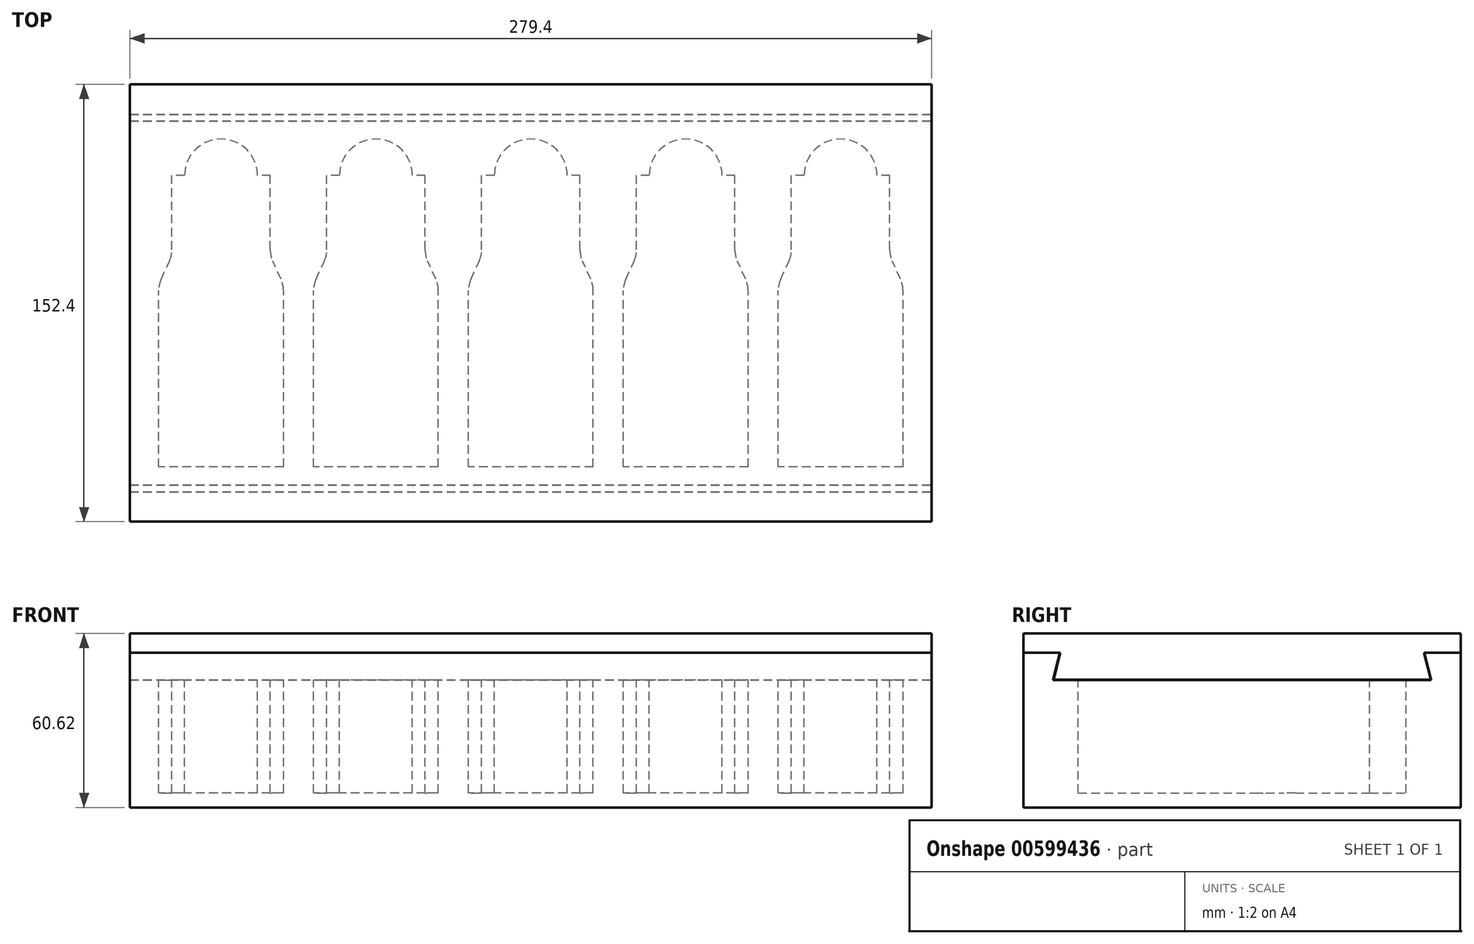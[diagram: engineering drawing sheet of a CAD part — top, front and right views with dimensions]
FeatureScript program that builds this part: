
annotation { "Feature Type Name" : "Feature", "Feature Type Description" : "" }
export const myFeature = defineFeature(function(context is Context, id is Id, definition is map)
    precondition{}
    {
        {
            var Q0;
            Q0=qCreatedBy(makeId("Top.planeOp"),FACE);
            var sketch = newSketch(context, id + "F0", { "sketchPlane" : qUnion([Q0])});
            skLineSegment(sketch, "E0.bottom", {"start": v(139.7, -76.2) * mm, "end": v(-139.7, -76.2) * mm});
            skLineSegment(sketch, "E0.top", {"start": v(139.7, 76.2) * mm, "end": v(-139.7, 76.2) * mm});
            skLineSegment(sketch, "E0.left", {"start": v(139.7, -76.2) * mm, "end": v(139.7, 76.2) * mm});
            skLineSegment(sketch, "E0.right", {"start": v(-139.7, -76.2) * mm, "end": v(-139.7, 76.2) * mm});
            skPoint(sketch, "E0.middle", {"position": v(0, 0) * mm});
            skSolve(sketch);
        }
        {
            var Q0;
            Q0=makeQuery(id+"F0.imprint","IMPRINT",FACE,{"disambiguationData":[TD([[makeQuery(id+"F0.imprint","IMPRINT",EDGE,{"derivedFrom":sQuery(id+"F0.wireOp",EDGE,"E0.bottom")}),-1.0]])]});
            extrude(context, id + "F1", {"entities" : qUnion([Q0]), "depth" : 53.97 * mm, "offsetDistance" : 25.4 * mm});
        }
        {
            var Q0;
            Q0=makeQuery(id+"F1.opExtrude","SWEPT_FACE",FACE,{"disambiguationData":[OSD([sQuery(id+"F0.wireOp",EDGE,"E0.left")])]});
            var sketch = newSketch(context, id + "F2", { "sketchPlane" : qUnion([Q0])});
            skLineSegment(sketch, "E1.top", {"start": v(-65.87, 44.45) * mm, "end": v(65.87, 44.45) * mm});
            skLineSegment(sketch, "E2.bottom", {"start": v(-63.5, 53.98) * mm, "end": v(63.5, 53.98) * mm});
            skLineSegment(sketch, "E3", {"start": v(-65.87, 44.45) * mm, "end": v(-63.5, 53.98) * mm});
            skLineSegment(sketch, "E4", {"start": v(65.87, 44.45) * mm, "end": v(63.5, 53.98) * mm});
            skLineSegment(sketch, "E5", {"start": v(-56.48, 75.32) * mm, "end": v(-56.48, 24.92) * mm, "construction": true});
            skLineSegment(sketch, "E6", {"start": v(-49.45, 53.98) * mm, "end": v(-47.08, 44.45) * mm, "construction": true});
            skSolve(sketch);
        }
        {
            var Q0;
            Q0=makeQuery(id+"F2.imprint","IMPRINT",FACE,{"disambiguationData":[TD([[makeQuery(id+"F2.imprint","IMPRINT",EDGE,{"derivedFrom":sQuery(id+"F2.wireOp",EDGE,"E1.top")}),1.0]])]});
            extrude(context, id + "F3", {"entities" : qUnion([Q0]), "operationType" : NewBodyOperationType.REMOVE, "endBound" : BoundingType.THROUGH_ALL, "oppositeDirection" : true, "depth" : 25.4 * mm, "offsetDistance" : 25.4 * mm});
        }
        {
            var Q0;
            Q0=makeQuery(id+"F3.boolean.opBoolean","COPY",FACE,{"derivedFrom":makeQuery(id+"F3.opExtrude","SWEPT_FACE",FACE,{"disambiguationData":[OSD([sQuery(id+"F2.wireOp",EDGE,"E1.top")])]})});
            var sketch = newSketch(context, id + "F4", { "sketchPlane" : qUnion([Q0])});
            skLineSegment(sketch, "E7.bottom", {"start": v(-86.2, -57.15) * mm, "end": v(-129.7, -57.15) * mm});
            skLineSegment(sketch, "E7.top", {"start": v(-90.8, 44.45) * mm, "end": v(-95.25, 44.45) * mm});
            skLineSegment(sketch, "E7.left", {"start": v(-86.2, -57.15) * mm, "end": v(-86.2, 4.3) * mm});
            skLineSegment(sketch, "E7.right", {"start": v(-129.7, -57.15) * mm, "end": v(-129.7, 4.3) * mm});
            skPoint(sketch, "E7.middle", {"position": v(-107.95, -6.35) * mm});
            skLineSegment(sketch, "E8", {"start": v(-107.95, -6.35) * mm, "end": v(-107.95, 97.87) * mm, "construction": true});
            skPoint(sketch, "E8.endSnap0", {"position": v(-107.95, 44.45) * mm});
            skLineSegment(sketch, "E9", {"start": v(-128.85, 8.22) * mm, "end": v(-125.94, 14.64) * mm});
            skLineSegment(sketch, "E10", {"start": v(-125.1, 18.57) * mm, "end": v(-125.1, 44.45) * mm});
            skPoint(sketch, "E11.orphan", {"position": v(-129.7, 44.45) * mm});
            skLineSegment(sketch, "E12.MirrorCS", {"start": v(-90.8, 18.57) * mm, "end": v(-90.8, 44.45) * mm});
            skLineSegment(sketch, "E13.MirrorCS", {"start": v(-87.05, 8.22) * mm, "end": v(-89.96, 14.64) * mm});
            skPoint(sketch, "E14.orphan", {"position": v(-86.2, 44.45) * mm});
            skPoint(sketch, "E15.visualSharp", {"position": v(-90.8, 16.51) * mm});
            skArc(sketch, "E15.filletArc", {"start": v(-90.8, 18.57) * mm, "mid": v(-90.6, 16.56) * mm, "end": v(-89.96, 14.64) * mm});
            skPoint(sketch, "E16.visualSharp", {"position": v(-86.2, 6.35) * mm});
            skArc(sketch, "E16.filletArc", {"start": v(-86.2, 4.3) * mm, "mid": v(-86.41, 6.3) * mm, "end": v(-87.05, 8.22) * mm});
            skPoint(sketch, "E17.visualSharp", {"position": v(-129.7, 6.35) * mm});
            skArc(sketch, "E17.filletArc", {"start": v(-128.85, 8.22) * mm, "mid": v(-129.49, 6.3) * mm, "end": v(-129.7, 4.3) * mm});
            skPoint(sketch, "E18.visualSharp", {"position": v(-125.1, 16.51) * mm});
            skArc(sketch, "E18.filletArc", {"start": v(-125.94, 14.64) * mm, "mid": v(-125.3, 16.56) * mm, "end": v(-125.1, 18.57) * mm});
            skPoint(sketch, "E19.1.0.0", {"position": v(-53.97, -6.35) * mm});
            skPoint(sketch, "E19.1.0.1", {"position": v(-36.83, 16.51) * mm});
            skLineSegment(sketch, "E19.1.0.2", {"start": v(-36.83, 44.45) * mm, "end": v(-41.27, 44.45) * mm});
            skLineSegment(sketch, "E19.1.0.3", {"start": v(-32.22, -57.15) * mm, "end": v(-32.22, 4.3) * mm});
            skLineSegment(sketch, "E19.1.0.4", {"start": v(-32.22, -57.15) * mm, "end": v(-75.73, -57.15) * mm});
            skLineSegment(sketch, "E19.1.0.5", {"start": v(-75.73, -57.15) * mm, "end": v(-75.73, 4.3) * mm});
            skLineSegment(sketch, "E19.1.0.6", {"start": v(-71.12, 18.57) * mm, "end": v(-71.12, 44.45) * mm});
            skLineSegment(sketch, "E19.1.0.7", {"start": v(-36.83, 18.57) * mm, "end": v(-36.83, 44.45) * mm});
            skPoint(sketch, "E19.1.0.8", {"position": v(-32.22, 6.35) * mm});
            skPoint(sketch, "E19.1.0.9", {"position": v(-32.22, 44.45) * mm});
            skPoint(sketch, "E19.1.0.10", {"position": v(-53.97, 44.45) * mm});
            skPoint(sketch, "E19.1.0.11", {"position": v(-71.12, 16.51) * mm});
            skArc(sketch, "E19.1.0.12", {"start": v(-74.88, 8.22) * mm, "mid": v(-75.51, 6.3) * mm, "end": v(-75.73, 4.3) * mm});
            skLineSegment(sketch, "E19.1.0.13", {"start": v(-74.88, 8.22) * mm, "end": v(-71.97, 14.64) * mm});
            skLineSegment(sketch, "E19.1.0.14", {"start": v(-33.07, 8.22) * mm, "end": v(-35.98, 14.64) * mm});
            skArc(sketch, "E19.1.0.15", {"start": v(-36.83, 18.57) * mm, "mid": v(-36.62, 16.56) * mm, "end": v(-35.98, 14.64) * mm});
            skArc(sketch, "E19.1.0.16", {"start": v(-71.97, 14.64) * mm, "mid": v(-71.33, 16.56) * mm, "end": v(-71.12, 18.57) * mm});
            skArc(sketch, "E19.1.0.17", {"start": v(-32.22, 4.3) * mm, "mid": v(-32.44, 6.3) * mm, "end": v(-33.07, 8.22) * mm});
            skPoint(sketch, "E19.2.0.0", {"position": v(0, -6.35) * mm});
            skPoint(sketch, "E19.2.0.1", {"position": v(17.14, 16.51) * mm});
            skLineSegment(sketch, "E19.2.0.2", {"start": v(17.14, 44.45) * mm, "end": v(12.7, 44.45) * mm});
            skLineSegment(sketch, "E19.2.0.3", {"start": v(21.75, -57.15) * mm, "end": v(21.75, 4.3) * mm});
            skLineSegment(sketch, "E19.2.0.4", {"start": v(21.75, -57.15) * mm, "end": v(-21.75, -57.15) * mm});
            skLineSegment(sketch, "E19.2.0.5", {"start": v(-21.75, -57.15) * mm, "end": v(-21.75, 4.3) * mm});
            skLineSegment(sketch, "E19.2.0.6", {"start": v(-17.14, 18.57) * mm, "end": v(-17.14, 44.45) * mm});
            skLineSegment(sketch, "E19.2.0.7", {"start": v(17.15, 18.57) * mm, "end": v(17.15, 44.45) * mm});
            skPoint(sketch, "E19.2.0.8", {"position": v(21.75, 6.35) * mm});
            skPoint(sketch, "E19.2.0.9", {"position": v(21.75, 44.45) * mm});
            skPoint(sketch, "E19.2.0.10", {"position": v(0, 44.45) * mm});
            skPoint(sketch, "E19.2.0.11", {"position": v(-17.14, 16.51) * mm});
            skArc(sketch, "E19.2.0.12", {"start": v(-20.9, 8.22) * mm, "mid": v(-21.54, 6.3) * mm, "end": v(-21.75, 4.3) * mm});
            skLineSegment(sketch, "E19.2.0.13", {"start": v(-20.9, 8.22) * mm, "end": v(-18, 14.64) * mm});
            skLineSegment(sketch, "E19.2.0.14", {"start": v(20.9, 8.22) * mm, "end": v(18, 14.64) * mm});
            skArc(sketch, "E19.2.0.15", {"start": v(17.14, 18.57) * mm, "mid": v(17.36, 16.56) * mm, "end": v(18, 14.64) * mm});
            skArc(sketch, "E19.2.0.16", {"start": v(-18, 14.64) * mm, "mid": v(-17.36, 16.56) * mm, "end": v(-17.14, 18.57) * mm});
            skArc(sketch, "E19.2.0.17", {"start": v(21.75, 4.3) * mm, "mid": v(21.54, 6.3) * mm, "end": v(20.9, 8.22) * mm});
            skPoint(sketch, "E19.3.0.0", {"position": v(53.97, -6.35) * mm});
            skPoint(sketch, "E19.3.0.1", {"position": v(71.12, 16.51) * mm});
            skLineSegment(sketch, "E19.3.0.2", {"start": v(71.12, 44.45) * mm, "end": v(66.68, 44.45) * mm});
            skLineSegment(sketch, "E19.3.0.3", {"start": v(75.73, -57.15) * mm, "end": v(75.73, 4.3) * mm});
            skLineSegment(sketch, "E19.3.0.4", {"start": v(75.73, -57.15) * mm, "end": v(32.22, -57.15) * mm});
            skLineSegment(sketch, "E19.3.0.5", {"start": v(32.22, -57.15) * mm, "end": v(32.22, 4.3) * mm});
            skLineSegment(sketch, "E19.3.0.6", {"start": v(36.83, 18.57) * mm, "end": v(36.83, 44.45) * mm});
            skLineSegment(sketch, "E19.3.0.7", {"start": v(71.12, 18.57) * mm, "end": v(71.12, 44.45) * mm});
            skPoint(sketch, "E19.3.0.8", {"position": v(75.73, 6.35) * mm});
            skPoint(sketch, "E19.3.0.9", {"position": v(75.73, 44.45) * mm});
            skPoint(sketch, "E19.3.0.10", {"position": v(53.97, 44.45) * mm});
            skPoint(sketch, "E19.3.0.11", {"position": v(36.83, 16.51) * mm});
            skArc(sketch, "E19.3.0.12", {"start": v(33.07, 8.22) * mm, "mid": v(32.44, 6.3) * mm, "end": v(32.22, 4.3) * mm});
            skLineSegment(sketch, "E19.3.0.13", {"start": v(33.07, 8.22) * mm, "end": v(35.98, 14.64) * mm});
            skLineSegment(sketch, "E19.3.0.14", {"start": v(74.88, 8.22) * mm, "end": v(71.97, 14.64) * mm});
            skArc(sketch, "E19.3.0.15", {"start": v(71.12, 18.57) * mm, "mid": v(71.33, 16.56) * mm, "end": v(71.97, 14.64) * mm});
            skArc(sketch, "E19.3.0.16", {"start": v(35.98, 14.64) * mm, "mid": v(36.62, 16.56) * mm, "end": v(36.83, 18.57) * mm});
            skArc(sketch, "E19.3.0.17", {"start": v(75.73, 4.3) * mm, "mid": v(75.51, 6.3) * mm, "end": v(74.88, 8.22) * mm});
            skPoint(sketch, "E19.4.0.0", {"position": v(107.95, -6.35) * mm});
            skPoint(sketch, "E19.4.0.1", {"position": v(125.1, 16.51) * mm});
            skLineSegment(sketch, "E19.4.0.2", {"start": v(125.1, 44.45) * mm, "end": v(120.65, 44.45) * mm});
            skLineSegment(sketch, "E19.4.0.3", {"start": v(129.7, -57.15) * mm, "end": v(129.7, 4.3) * mm});
            skLineSegment(sketch, "E19.4.0.4", {"start": v(129.7, -57.15) * mm, "end": v(86.2, -57.15) * mm});
            skLineSegment(sketch, "E19.4.0.5", {"start": v(86.2, -57.15) * mm, "end": v(86.2, 4.3) * mm});
            skLineSegment(sketch, "E19.4.0.6", {"start": v(90.8, 18.57) * mm, "end": v(90.8, 44.45) * mm});
            skLineSegment(sketch, "E19.4.0.7", {"start": v(125.1, 18.57) * mm, "end": v(125.1, 44.45) * mm});
            skPoint(sketch, "E19.4.0.8", {"position": v(129.7, 6.35) * mm});
            skPoint(sketch, "E19.4.0.9", {"position": v(129.7, 44.45) * mm});
            skPoint(sketch, "E19.4.0.10", {"position": v(107.95, 44.45) * mm});
            skPoint(sketch, "E19.4.0.11", {"position": v(90.8, 16.51) * mm});
            skArc(sketch, "E19.4.0.12", {"start": v(87.05, 8.22) * mm, "mid": v(86.41, 6.3) * mm, "end": v(86.2, 4.3) * mm});
            skLineSegment(sketch, "E19.4.0.13", {"start": v(87.05, 8.22) * mm, "end": v(89.96, 14.64) * mm});
            skLineSegment(sketch, "E19.4.0.14", {"start": v(128.85, 8.22) * mm, "end": v(125.94, 14.64) * mm});
            skArc(sketch, "E19.4.0.15", {"start": v(125.1, 18.57) * mm, "mid": v(125.3, 16.56) * mm, "end": v(125.94, 14.64) * mm});
            skArc(sketch, "E19.4.0.16", {"start": v(89.96, 14.64) * mm, "mid": v(90.6, 16.56) * mm, "end": v(90.8, 18.57) * mm});
            skArc(sketch, "E19.4.0.17", {"start": v(129.7, 4.3) * mm, "mid": v(129.49, 6.3) * mm, "end": v(128.85, 8.22) * mm});
            skLineSegment(sketch, "E19.direction1", {"start": v(-129.7, -57.15) * mm, "end": v(-75.73, -57.15) * mm, "construction": true});
            skArc(sketch, "E20", {"start": v(-95.25, 44.45) * mm, "mid": v(-107.95, 57.15) * mm, "end": v(-120.65, 44.45) * mm});
            skLineSegment(sketch, "E21.trimOffspring", {"start": v(-120.65, 44.45) * mm, "end": v(-125.1, 44.45) * mm});
            skArc(sketch, "E22.1.0.0", {"start": v(-41.27, 44.45) * mm, "mid": v(-53.98, 57.15) * mm, "end": v(-66.67, 44.45) * mm});
            skArc(sketch, "E22.2.0.0", {"start": v(12.7, 44.45) * mm, "mid": v(0, 57.15) * mm, "end": v(-12.7, 44.45) * mm});
            skArc(sketch, "E22.3.0.0", {"start": v(66.68, 44.45) * mm, "mid": v(53.98, 57.15) * mm, "end": v(41.28, 44.45) * mm});
            skArc(sketch, "E22.4.0.0", {"start": v(120.65, 44.45) * mm, "mid": v(107.95, 57.15) * mm, "end": v(95.25, 44.45) * mm});
            skLineSegment(sketch, "E22.direction1", {"start": v(-120.65, 44.45) * mm, "end": v(-66.67, 44.45) * mm, "construction": true});
            skLineSegment(sketch, "E23.trimOffspring", {"start": v(-66.67, 44.45) * mm, "end": v(-71.12, 44.45) * mm});
            skLineSegment(sketch, "E24.trimOffspring", {"start": v(-12.7, 44.45) * mm, "end": v(-17.14, 44.45) * mm});
            skLineSegment(sketch, "E25.trimOffspring", {"start": v(41.28, 44.45) * mm, "end": v(36.83, 44.45) * mm});
            skLineSegment(sketch, "E26.trimOffspring", {"start": v(95.25, 44.45) * mm, "end": v(90.8, 44.45) * mm});
            skSolve(sketch);
        }
        {
            var Q0;
            Q0 = qSketchRegion(id + "F4", true);
            extrude(context, id + "F5", {"entities" : qUnion([Q0]), "operationType" : NewBodyOperationType.REMOVE, "oppositeDirection" : true, "depth" : 39.37 * mm, "offsetDistance" : 25.4 * mm});
        }
        {
            var Q0;
            Q0=makeQuery(id+"F1.opExtrude","SWEPT_FACE",FACE,{"disambiguationData":[OSD([sQuery(id+"F0.wireOp",EDGE,"E0.left")])]});
            var sketch = newSketch(context, id + "F6", { "sketchPlane" : qUnion([Q0])});
            skLineSegment(sketch, "E27.bottom", {"start": v(-76.2, 53.98) * mm, "end": v(-63.37, 53.98) * mm});
            skLineSegment(sketch, "E27.top", {"start": v(-76.2, 60.62) * mm, "end": v(76.2, 60.62) * mm});
            skLineSegment(sketch, "E27.left", {"start": v(-76.2, 53.98) * mm, "end": v(-76.2, 60.62) * mm});
            skLineSegment(sketch, "E27.right", {"start": v(76.2, 53.98) * mm, "end": v(76.2, 60.62) * mm});
            skLineSegment(sketch, "E28.trimOffspring", {"start": v(63.37, 53.98) * mm, "end": v(76.2, 53.98) * mm});
            skLineSegment(sketch, "E29.top", {"start": v(-65.71, 44.58) * mm, "end": v(65.71, 44.58) * mm});
            skLineSegment(sketch, "E30", {"start": v(-63.37, 53.98) * mm, "end": v(-65.71, 44.58) * mm});
            skLineSegment(sketch, "E31", {"start": v(63.37, 53.98) * mm, "end": v(65.71, 44.58) * mm});
            skLineSegment(sketch, "E32", {"start": v(-82.17, 53.98) * mm, "end": v(-79.82, 44.58) * mm, "construction": true});
            skLineSegment(sketch, "E33", {"start": v(-72.77, 50.94) * mm, "end": v(-72.77, 14.67) * mm, "construction": true});
            skSolve(sketch);
        }
        {
            var Q0;
            Q0=makeQuery(id+"F6.imprint","IMPRINT",FACE,{"disambiguationData":[TD([[makeQuery(id+"F6.imprint","IMPRINT",EDGE,{"derivedFrom":sQuery(id+"F6.wireOp",EDGE,"E27.top")}),-1.0]])]});
            var Q1;
            Q1=makeQuery(id+"F1.opExtrude","SWEPT_FACE",FACE,{"disambiguationData":[OSD([sQuery(id+"F0.wireOp",EDGE,"E0.right")])]});
            extrude(context, id + "F7", {"entities" : qUnion([Q0]), "endBound" : BoundingType.UP_TO_SURFACE, "oppositeDirection" : true, "depth" : 25.4 * mm, "endBoundEntityFace" : qUnion([Q1]), "offsetDistance" : 25.4 * mm});
        }
    });
